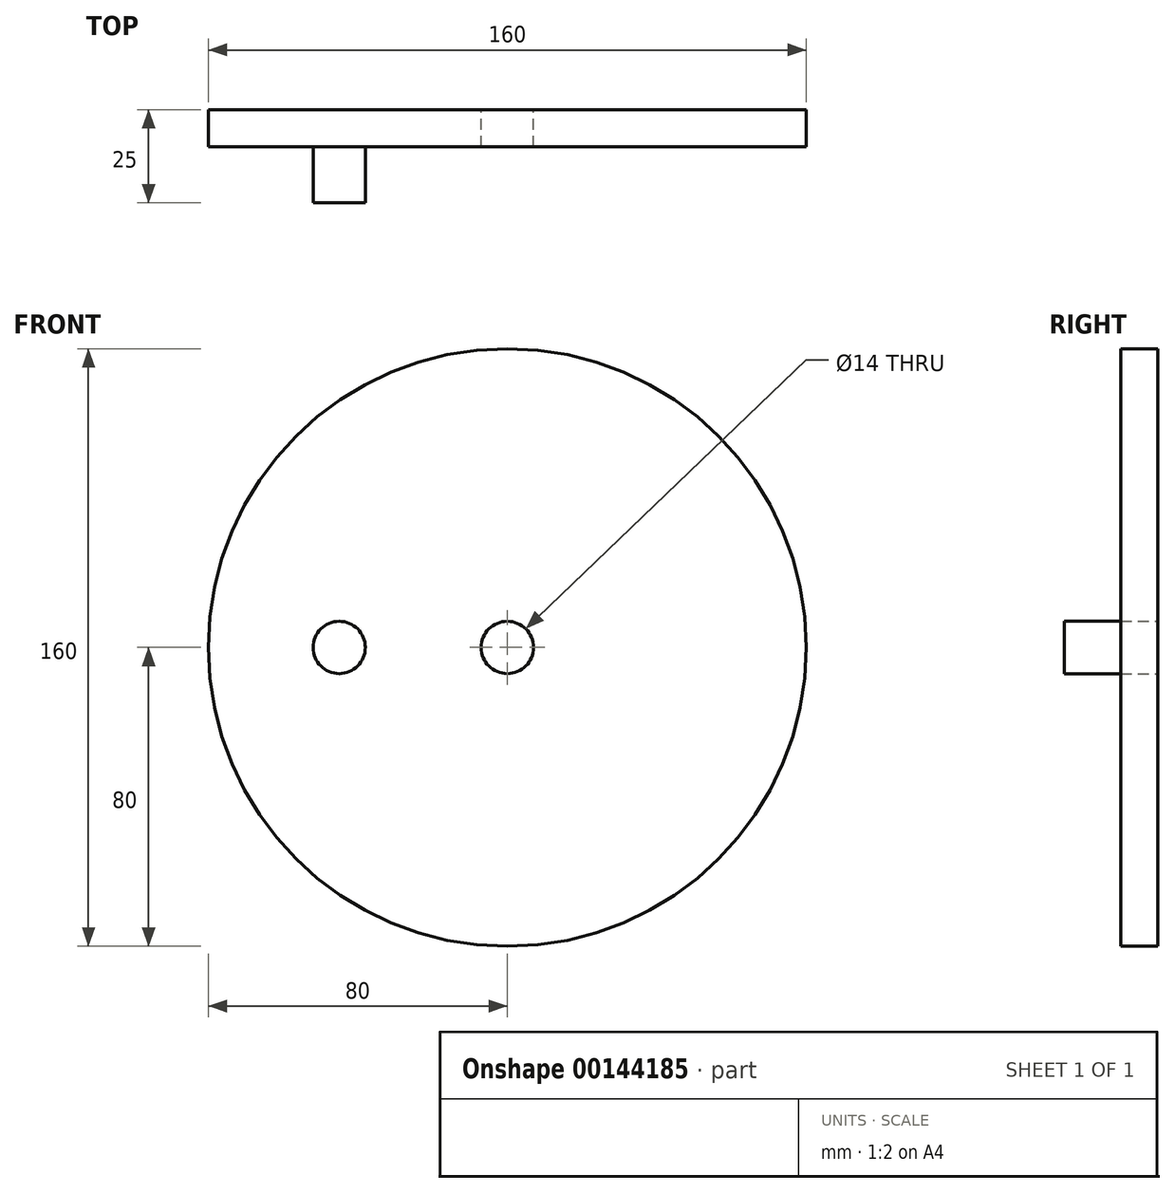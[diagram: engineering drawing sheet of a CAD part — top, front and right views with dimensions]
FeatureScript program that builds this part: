
annotation { "Feature Type Name" : "Feature", "Feature Type Description" : "" }
export const myFeature = defineFeature(function(context is Context, id is Id, definition is map)
    precondition{}
    {
        {
            var Q0;
            Q0=qCreatedBy(makeId("Front.planeOp"),FACE);
            var sketch = newSketch(context, id + "F0", { "sketchPlane" : qUnion([Q0])});
            skCircle(sketch, "E0", {"center": v(0, 0) * mm, "radius": 80 * mm});
            skCircle(sketch, "E1", {"center": v(0, 0) * mm, "radius": 7 * mm});
            skPoint(sketch, "E2", {"position": v(0, 50) * mm});
            skPoint(sketch, "E3", {"position": v(-50, 0) * mm});
            skPoint(sketch, "E4", {"position": v(50, 0) * mm});
            skPoint(sketch, "E5", {"position": v(0, -50) * mm});
            skSolve(sketch);
        }
        {
            var Q0;
            Q0 = qSketchRegion(id + "F0", true);
            extrude(context, id + "F1", {"entities" : qUnion([Q0]), "depth" : 10 * mm});
        }
        {
            var Q0;
            Q0=qCreatedBy(makeId("Front.planeOp"),FACE);
            var sketch = newSketch(context, id + "F2", { "sketchPlane" : qUnion([Q0])});
            skCircle(sketch, "E6", {"center": v(-45, 0) * mm, "radius": 7 * mm});
            skSolve(sketch);
        }
        {
            var Q0;
            Q0 = qSketchRegion(id + "F2", true);
            extrude(context, id + "F3", {"entities" : qUnion([Q0]), "operationType" : NewBodyOperationType.ADD, "depth" : 25 * mm});
        }
    });
